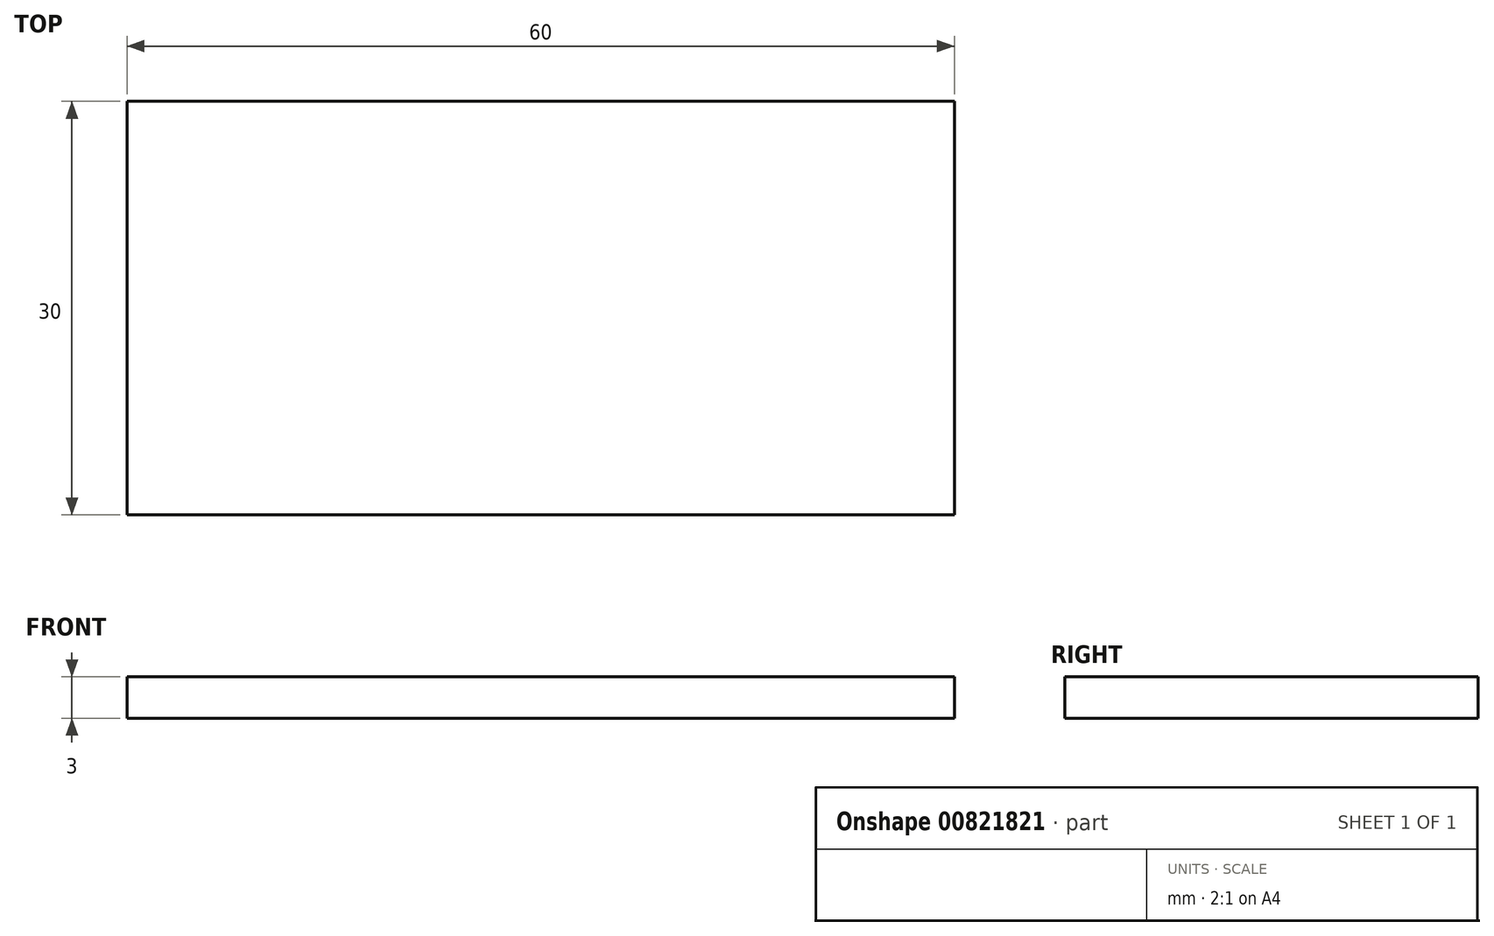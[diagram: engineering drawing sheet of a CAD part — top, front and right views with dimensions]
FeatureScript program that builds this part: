
annotation { "Feature Type Name" : "Feature", "Feature Type Description" : "" }
export const myFeature = defineFeature(function(context is Context, id is Id, definition is map)
    precondition{}
    {
        {
            var Q0;
            Q0=qCreatedBy(makeId("Top.planeOp"),FACE);
            var sketch = newSketch(context, id + "F0", { "sketchPlane" : qUnion([Q0])});
            skLineSegment(sketch, "E0.bottom", {"start": v(30, 15) * mm, "end": v(-30, 15) * mm});
            skLineSegment(sketch, "E0.top", {"start": v(30, -15) * mm, "end": v(-30, -15) * mm});
            skLineSegment(sketch, "E0.left", {"start": v(30, 15) * mm, "end": v(30, -15) * mm});
            skLineSegment(sketch, "E0.right", {"start": v(-30, 15) * mm, "end": v(-30, -15) * mm});
            skPoint(sketch, "E0.middle", {"position": v(0, 0) * mm});
            skSolve(sketch);
        }
        {
            var Q0;
            Q0=makeQuery(id+"F0.imprint","IMPRINT",FACE,{"disambiguationData":[TD([[makeQuery(id+"F0.imprint","IMPRINT",EDGE,{"derivedFrom":sQuery(id+"F0.wireOp",EDGE,"E0.bottom")}),1.0]])]});
            extrude(context, id + "F1", {"entities" : qUnion([Q0]), "depth" : 3 * mm, "offsetDistance" : 25 * mm});
        }
    });
